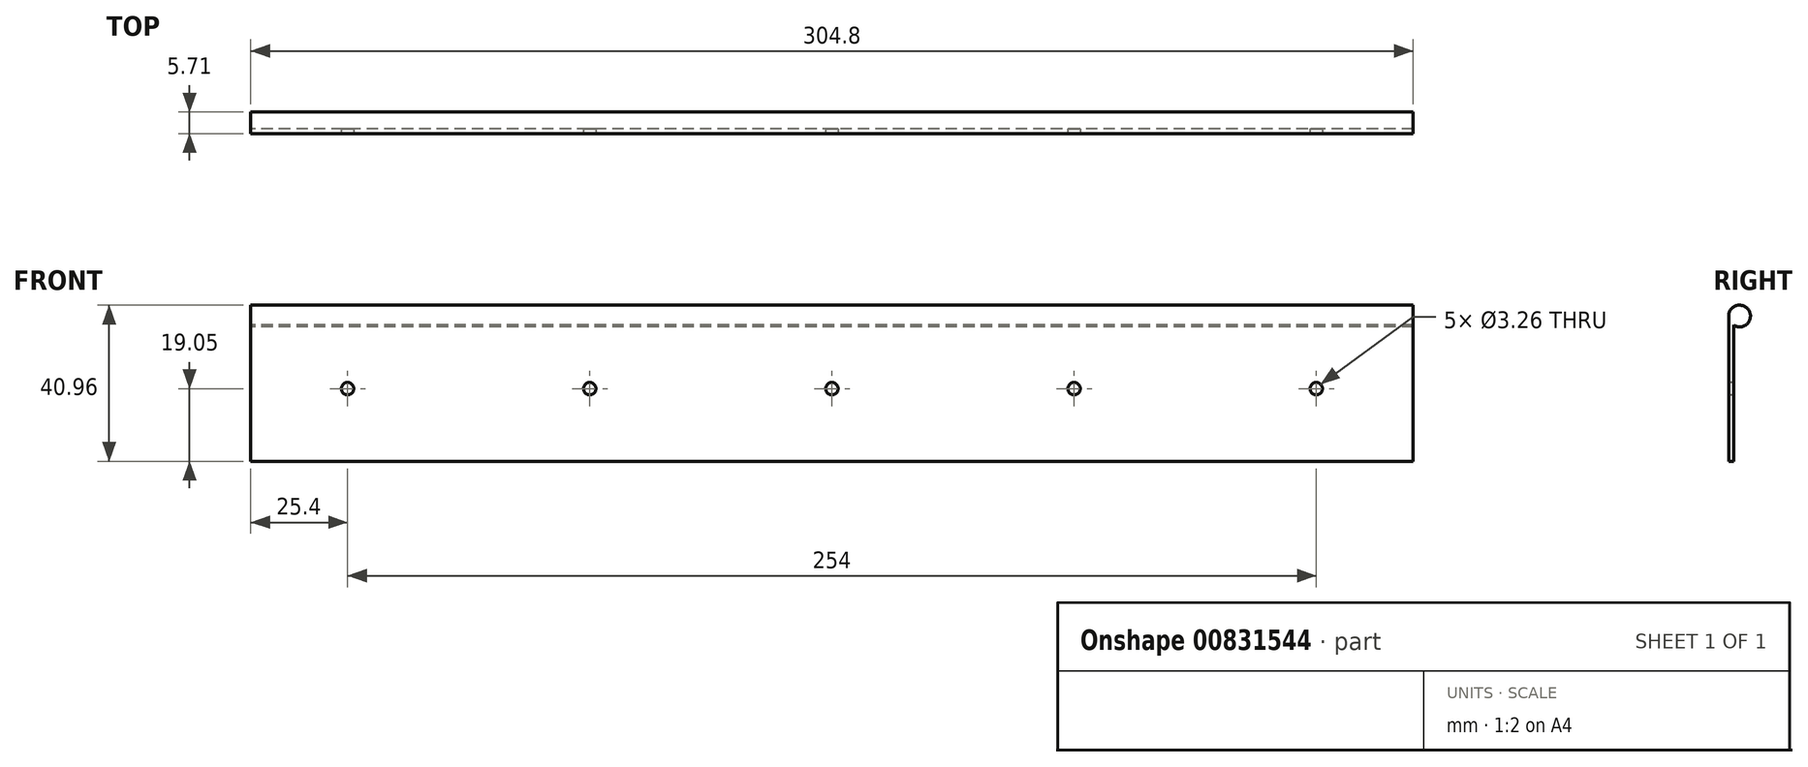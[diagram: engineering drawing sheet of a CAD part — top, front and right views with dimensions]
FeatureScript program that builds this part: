
annotation { "Feature Type Name" : "Feature", "Feature Type Description" : "" }
export const myFeature = defineFeature(function(context is Context, id is Id, definition is map)
    precondition{}
    {
        {
            var Q0;
            Q0=qCreatedBy(makeId("Right.planeOp"),FACE);
            var sketch = newSketch(context, id + "F0", { "sketchPlane" : qUnion([Q0])});
            skLineSegment(sketch, "E0.bottom", {"start": v(0, 0) * mm, "end": v(1.27, 0) * mm});
            skLineSegment(sketch, "E0.left", {"start": v(0, 0) * mm, "end": v(0, 38.1) * mm});
            skLineSegment(sketch, "E0.right", {"start": v(1.27, 0) * mm, "end": v(1.27, 35.72) * mm});
            skCircle(sketch, "E1", {"center": v(2.86, 38.1) * mm, "radius": 2.86 * mm, "construction": true});
            skPoint(sketch, "E1.centerSnap0", {"position": v(1.45, 38.1) * mm});
            skArc(sketch, "E2", {"start": v(1.27, 35.72) * mm, "mid": v(5.38, 39.45) * mm, "end": v(0, 38.1) * mm});
            skSolve(sketch);
        }
        {
            var Q0;
            Q0=qSketchRegion(id+"F0",true);
            extrude(context, id + "F1", {"entities" : qUnion([Q0]), "depth" : 304.8 * mm, "offsetDistance" : 25.4 * mm});
        }
        {
            var Q0;
            Q0=makeQuery(id+"F1.opExtrude","SWEPT_FACE",FACE,{"disambiguationData":[OSD([sQuery(id+"F0.wireOp",EDGE,"E0.left")])]});
            var sketch = newSketch(context, id + "F2", { "sketchPlane" : qUnion([Q0])});
            skPoint(sketch, "E3", {"position": v(88.9, 19.05) * mm});
            skPoint(sketch, "E4", {"position": v(152.4, 19.05) * mm});
            skPoint(sketch, "E5", {"position": v(215.9, 19.05) * mm});
            skPoint(sketch, "E6", {"position": v(25.4, 19.05) * mm});
            skPoint(sketch, "E7", {"position": v(279.4, 19.05) * mm});
            skLineSegment(sketch, "E8", {"start": v(0, 19.05) * mm, "end": v(25.4, 19.05) * mm});
            skLineSegment(sketch, "E9", {"start": v(25.4, 19.05) * mm, "end": v(88.9, 19.05) * mm});
            skLineSegment(sketch, "E10", {"start": v(88.9, 19.05) * mm, "end": v(152.4, 19.05) * mm});
            skLineSegment(sketch, "E11", {"start": v(152.4, 19.05) * mm, "end": v(215.9, 19.05) * mm});
            skLineSegment(sketch, "E12", {"start": v(215.9, 19.05) * mm, "end": v(279.4, 19.05) * mm});
            skLineSegment(sketch, "E13", {"start": v(279.4, 19.05) * mm, "end": v(304.8, 19.05) * mm});
            skSolve(sketch);
        }
        {
            var Q0;
            Q0=sQuery(id+"F2.wireOp",VERTEX,"E6");
            var Q1;
            Q1=sQuery(id+"F2.wireOp",VERTEX,"E3");
            var Q2;
            Q2=sQuery(id+"F2.wireOp",VERTEX,"E4");
            var Q3;
            Q3=sQuery(id+"F2.wireOp",VERTEX,"E5");
            var Q4;
            Q4=sQuery(id+"F2.wireOp",VERTEX,"E7");
            var Q5;
            Q5=makeQuery(id+"F1.opExtrude","SWEPT_BODY",BODY,{"disambiguationData":[OSD([sQuery(id+"F0.wireOp",EDGE,"E0.bottom"),sQuery(id+"F0.wireOp",EDGE,"E0.left"),sQuery(id+"F0.wireOp",EDGE,"E0.right"),sQuery(id+"F0.wireOp",EDGE,"E2")])]});
            hole(context, id + "F3", {"style" : HoleStyle.SIMPLE, "endStyle" : HoleEndStyle.THROUGH, "standardTappedOrClearance" : lookupTablePath({ "standard" : "ANSI", "size" : "#30 (0.13)", "type" : "Drilled" }), "standardBlindInLast" : lookupTablePath({ "standard" : "ANSI", "size" : "#30", "type" : "Drilled" }), "holeDiameter" : 3.26 * mm, "majorDiameter" : 6.35 * mm, "isTappedThrough" : true, "tappedDepth" : 12.7 * mm, "tapClearance" : 3, "locations" : qUnion([Q0, Q1, Q2, Q3, Q4]), "scope" : qUnion([Q5])});
        }
    });
